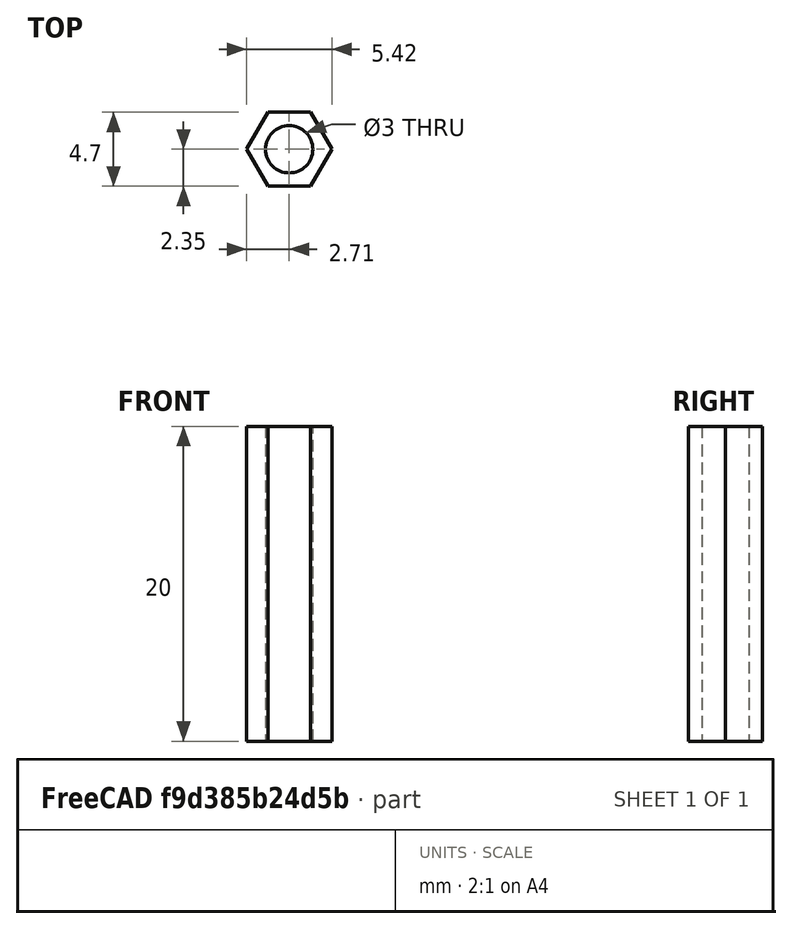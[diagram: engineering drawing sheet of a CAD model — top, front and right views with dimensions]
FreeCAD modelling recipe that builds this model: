
FCSTD DOCUMENT  (FreeCAD 0.18.4R)
Label: coxial_M3_20mm
License: All rights reserved
LicenseURL: http://en.wikipedia.org/wiki/All_rights_reserved
objects: Sketcher::SketchObject×1, PartDesign::Pad×1, PartDesign::Body×1
note: 4 computed .brp shape members not serialized (recipe doc carries the construction recipe); baked Part::Feature solids carry a one-line shape summary decoded from their .brp

FEATURE [Sketcher::SketchObject] Sketch
  MapMode = 5
  Support = -> [XY_Plane]
  sketch-geometry (8):
    g0: Circle CenterX=0 CenterY=0 CenterZ=0 NormalX=0 NormalY=0 NormalZ=1 AngleXU=0 Radius=1.5
    g1: LineSegment StartX=1.35677 StartY=-2.35 StartZ=0 EndX=2.71355 EndY=3.3862e-12 EndZ=0
    g2: LineSegment StartX=2.71355 StartY=3.3862e-12 StartZ=0 EndX=1.35677 EndY=2.35 EndZ=0
    g3: LineSegment StartX=1.35677 StartY=2.35 StartZ=0 EndX=-1.35677 EndY=2.35 EndZ=0
    g4: LineSegment StartX=-1.35677 StartY=2.35 StartZ=0 EndX=-2.71355 EndY=-3.27134e-11 EndZ=0
    g5: LineSegment StartX=-2.71355 StartY=-3.27134e-11 StartZ=0 EndX=-1.35677 EndY=-2.35 EndZ=0
    g6: LineSegment StartX=-1.35677 StartY=-2.35 StartZ=0 EndX=1.35677 EndY=-2.35 EndZ=0
    g7: Circle [constr] CenterX=0 CenterY=0 CenterZ=0 NormalX=0 NormalY=0 NormalZ=1 AngleXU=0 Radius=2.71355
  constraints (18):
    c: Radius(g0) = 1.5
    c: Coincident(g0,g-1)
    c: Coincident(g1,g2)
    c: Coincident(g2,g3)
    c: Coincident(g3,g4)
    c: Coincident(g4,g5)
    c: Coincident(g5,g6)
    c: Coincident(g6,g1)
    c: Equal(g1, g2-g6) x5
    c: PointOnObject(g1,g7)
    c: PointOnObject(g2,g7)
    c: PointOnObject(g3,g7)
    c: PointOnObject(g4,g7)
    c: PointOnObject(g5,g7)
    c: PointOnObject(g6,g7)
    c: Coincident(g7,g0)
    c: Distance(g2,g4) = 4.7
    c: Horizontal(g3)
FEATURE [PartDesign::Pad] Pad
  Length = 20
  Length2 = 100
  Profile = -> Sketch
  Type = 0
FEATURE [PartDesign::Body] Body
  Group = -> [Sketch,Pad]
  Origin = -> Origin
  Tip = -> Pad
